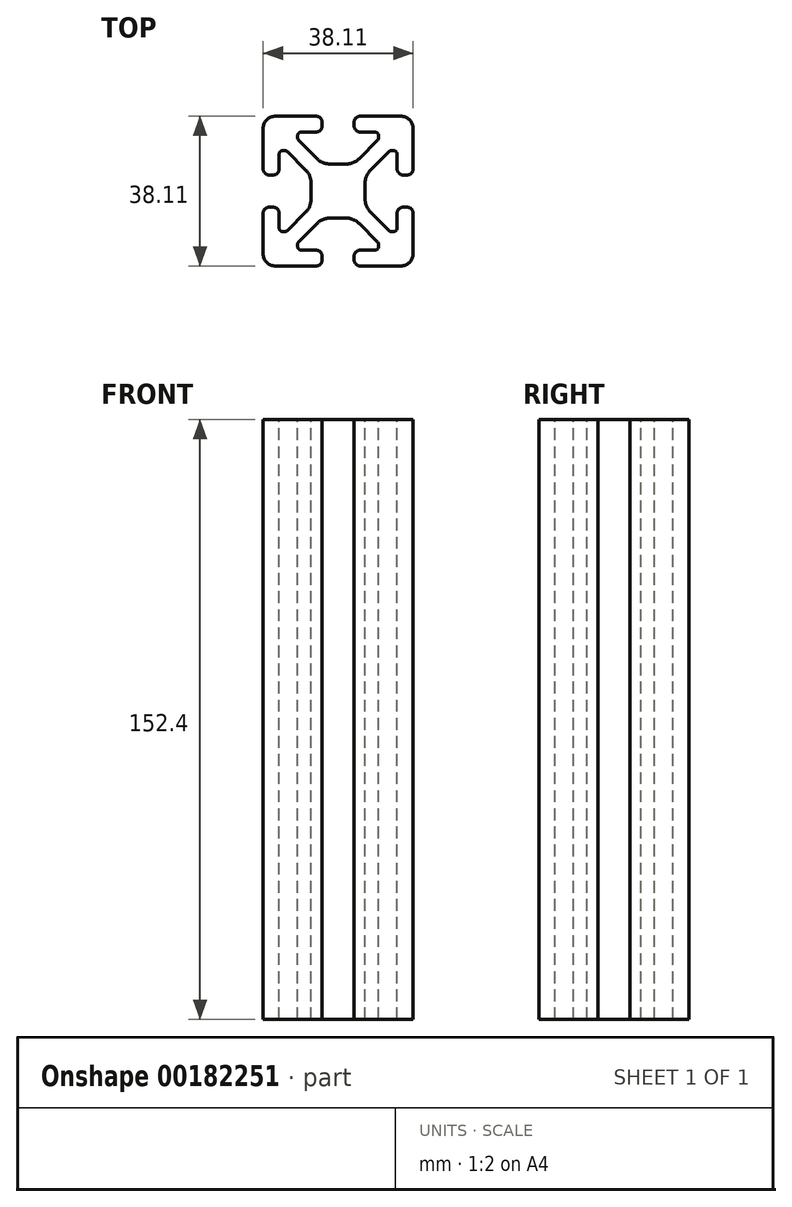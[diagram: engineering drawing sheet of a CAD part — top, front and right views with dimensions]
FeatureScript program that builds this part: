
annotation { "Feature Type Name" : "Feature", "Feature Type Description" : "" }
export const myFeature = defineFeature(function(context is Context, id is Id, definition is map)
    precondition{}
    {
        {
            var Q0;
            Q0=qCreatedBy(makeId("Top.planeOp"),FACE);
            var sketch = newSketch(context, id + "F0", { "sketchPlane" : qUnion([Q0])});
            skLineSegment(sketch, "E0.0", {"start": v(-3.18, 31.75) * mm, "end": v(-3.18, 21.51) * mm});
            skArc(sketch, "E1.0", {"start": v(0, 34.93) * mm, "mid": v(-2.25, 34) * mm, "end": v(-3.18, 31.75) * mm});
            skArc(sketch, "E2.0", {"start": v(-3.18, 21.51) * mm, "mid": v(-2.71, 20.4) * mm, "end": v(-1.6, 19.94) * mm});
            skLineSegment(sketch, "E3.0", {"start": v(-1.6, 19.94) * mm, "end": v(-0.69, 19.94) * mm});
            skArc(sketch, "E4.0", {"start": v(-0.69, 19.94) * mm, "mid": v(0.43, 20.4) * mm, "end": v(0.89, 21.51) * mm});
            skLineSegment(sketch, "E5.0", {"start": v(0.89, 21.51) * mm, "end": v(0.89, 25.27) * mm});
            skArc(sketch, "E6.0", {"start": v(0.89, 25.27) * mm, "mid": v(1.15, 25.9) * mm, "end": v(1.78, 26.16) * mm});
            skLineSegment(sketch, "E7.0", {"start": v(1.78, 26.16) * mm, "end": v(2.35, 26.16) * mm});
            skArc(sketch, "E8.0", {"start": v(2.35, 26.16) * mm, "mid": v(2.69, 26.1) * mm, "end": v(2.97, 25.9) * mm});
            skLineSegment(sketch, "E9.0", {"start": v(2.97, 25.9) * mm, "end": v(7.61, 21.26) * mm});
            skArc(sketch, "E10.0", {"start": v(7.61, 21.26) * mm, "mid": v(8.64, 19.72) * mm, "end": v(9, 17.9) * mm});
            skLineSegment(sketch, "E11.0", {"start": v(9, 17.9) * mm, "end": v(9, 13.85) * mm});
            skArc(sketch, "E12.0", {"start": v(9, 13.85) * mm, "mid": v(8.64, 12.03) * mm, "end": v(7.61, 10.49) * mm});
            skLineSegment(sketch, "E13.0", {"start": v(7.61, 10.49) * mm, "end": v(2.97, 5.85) * mm});
            skArc(sketch, "E14.0", {"start": v(2.97, 5.85) * mm, "mid": v(2.69, 5.66) * mm, "end": v(2.35, 5.59) * mm});
            skLineSegment(sketch, "E15.0", {"start": v(2.35, 5.59) * mm, "end": v(1.78, 5.59) * mm});
            skArc(sketch, "E16.0", {"start": v(1.78, 5.59) * mm, "mid": v(1.15, 5.85) * mm, "end": v(0.89, 6.48) * mm});
            skLineSegment(sketch, "E17.0", {"start": v(0.89, 6.48) * mm, "end": v(0.89, 10.24) * mm});
            skArc(sketch, "E18.0", {"start": v(0.89, 10.24) * mm, "mid": v(0.43, 11.35) * mm, "end": v(-0.69, 11.81) * mm});
            skLineSegment(sketch, "E19.0", {"start": v(-0.69, 11.81) * mm, "end": v(-1.6, 11.81) * mm});
            skArc(sketch, "E20.0", {"start": v(-1.6, 11.81) * mm, "mid": v(-2.71, 11.35) * mm, "end": v(-3.17, 10.24) * mm});
            skLineSegment(sketch, "E21.0", {"start": v(-3.17, 10.24) * mm, "end": v(-3.17, 0) * mm});
            skArc(sketch, "E22.0", {"start": v(-3.17, 0) * mm, "mid": v(-2.25, -2.25) * mm, "end": v(0, -3.17) * mm});
            skLineSegment(sketch, "E23.0", {"start": v(0, -3.17) * mm, "end": v(10.24, -3.17) * mm});
            skArc(sketch, "E24.0", {"start": v(10.24, -3.17) * mm, "mid": v(11.35, -2.71) * mm, "end": v(11.81, -1.6) * mm});
            skLineSegment(sketch, "E25.0", {"start": v(11.81, -1.6) * mm, "end": v(11.81, -0.69) * mm});
            skArc(sketch, "E26.0", {"start": v(11.81, -0.69) * mm, "mid": v(11.35, 0.43) * mm, "end": v(10.24, 0.89) * mm});
            skLineSegment(sketch, "E27.0", {"start": v(10.24, 0.89) * mm, "end": v(6.48, 0.89) * mm});
            skArc(sketch, "E28.0", {"start": v(6.48, 0.89) * mm, "mid": v(5.85, 1.15) * mm, "end": v(5.59, 1.78) * mm});
            skLineSegment(sketch, "E29.0", {"start": v(5.59, 1.78) * mm, "end": v(5.59, 2.35) * mm});
            skArc(sketch, "E30.0", {"start": v(5.59, 2.35) * mm, "mid": v(5.66, 2.69) * mm, "end": v(5.85, 2.97) * mm});
            skLineSegment(sketch, "E31.0", {"start": v(5.85, 2.97) * mm, "end": v(10.49, 7.61) * mm});
            skArc(sketch, "E32.0", {"start": v(10.49, 7.61) * mm, "mid": v(12.03, 8.64) * mm, "end": v(13.85, 9) * mm});
            skLineSegment(sketch, "E33.0", {"start": v(13.85, 9) * mm, "end": v(17.9, 9) * mm});
            skArc(sketch, "E34.0", {"start": v(17.9, 9) * mm, "mid": v(19.72, 8.64) * mm, "end": v(21.26, 7.61) * mm});
            skLineSegment(sketch, "E35.0", {"start": v(21.26, 7.61) * mm, "end": v(25.9, 2.97) * mm});
            skArc(sketch, "E36.0", {"start": v(25.9, 2.97) * mm, "mid": v(26.1, 2.69) * mm, "end": v(26.16, 2.35) * mm});
            skPoint(sketch, "E37.0", {"position": v(26.16, 1.78) * mm});
            skArc(sketch, "E38.0", {"start": v(26.16, 1.78) * mm, "mid": v(25.9, 1.15) * mm, "end": v(25.27, 0.89) * mm});
            skLineSegment(sketch, "E39.0", {"start": v(25.27, 0.89) * mm, "end": v(21.51, 0.89) * mm});
            skArc(sketch, "E40.0", {"start": v(21.51, 0.89) * mm, "mid": v(20.4, 0.43) * mm, "end": v(19.94, -0.69) * mm});
            skPoint(sketch, "E41.0", {"position": v(19.94, -1.6) * mm});
            skLineSegment(sketch, "E42.0", {"start": v(19.94, -0.69) * mm, "end": v(19.94, -1.6) * mm});
            skArc(sketch, "E43.0", {"start": v(19.94, -1.6) * mm, "mid": v(20.4, -2.71) * mm, "end": v(21.51, -3.17) * mm});
            skLineSegment(sketch, "E44.0", {"start": v(21.51, -3.17) * mm, "end": v(31.75, -3.17) * mm});
            skArc(sketch, "E45.0", {"start": v(31.75, -3.17) * mm, "mid": v(34, -2.25) * mm, "end": v(34.93, 0) * mm});
            skLineSegment(sketch, "E46.0", {"start": v(34.93, 0) * mm, "end": v(34.93, 10.24) * mm});
            skArc(sketch, "E47.0", {"start": v(34.93, 10.24) * mm, "mid": v(34.46, 11.35) * mm, "end": v(33.35, 11.81) * mm});
            skLineSegment(sketch, "E48.0", {"start": v(33.35, 11.81) * mm, "end": v(32.44, 11.81) * mm});
            skArc(sketch, "E49.0", {"start": v(32.44, 11.81) * mm, "mid": v(31.32, 11.35) * mm, "end": v(30.86, 10.24) * mm});
            skLineSegment(sketch, "E50.0", {"start": v(30.86, 10.24) * mm, "end": v(30.86, 6.48) * mm});
            skArc(sketch, "E51.0", {"start": v(30.86, 6.48) * mm, "mid": v(30.6, 5.85) * mm, "end": v(29.97, 5.59) * mm});
            skLineSegment(sketch, "E52.0", {"start": v(29.97, 5.59) * mm, "end": v(29.4, 5.59) * mm});
            skArc(sketch, "E53.0", {"start": v(29.4, 5.59) * mm, "mid": v(29.06, 5.66) * mm, "end": v(28.78, 5.85) * mm});
            skLineSegment(sketch, "E54.0", {"start": v(28.78, 5.85) * mm, "end": v(24.14, 10.49) * mm});
            skArc(sketch, "E55.0", {"start": v(24.14, 10.49) * mm, "mid": v(23.1, 12.03) * mm, "end": v(22.74, 13.85) * mm});
            skLineSegment(sketch, "E56.0", {"start": v(22.74, 13.85) * mm, "end": v(22.74, 17.9) * mm});
            skArc(sketch, "E57.0", {"start": v(22.74, 17.9) * mm, "mid": v(23.1, 19.72) * mm, "end": v(24.14, 21.26) * mm});
            skLineSegment(sketch, "E58.0", {"start": v(24.14, 21.26) * mm, "end": v(28.78, 25.9) * mm});
            skArc(sketch, "E59.0", {"start": v(28.78, 25.9) * mm, "mid": v(29.06, 26.1) * mm, "end": v(29.4, 26.16) * mm});
            skLineSegment(sketch, "E60.0", {"start": v(29.4, 26.16) * mm, "end": v(29.97, 26.16) * mm});
            skArc(sketch, "E61.0", {"start": v(29.97, 26.16) * mm, "mid": v(30.6, 25.9) * mm, "end": v(30.86, 25.27) * mm});
            skLineSegment(sketch, "E62.0", {"start": v(30.86, 25.27) * mm, "end": v(30.86, 21.51) * mm});
            skArc(sketch, "E63.0", {"start": v(30.86, 21.51) * mm, "mid": v(31.32, 20.4) * mm, "end": v(32.44, 19.94) * mm});
            skLineSegment(sketch, "E64.0", {"start": v(32.44, 19.94) * mm, "end": v(33.35, 19.94) * mm});
            skArc(sketch, "E65.0", {"start": v(33.35, 19.94) * mm, "mid": v(34.46, 20.4) * mm, "end": v(34.93, 21.51) * mm});
            skLineSegment(sketch, "E66.0", {"start": v(34.93, 21.51) * mm, "end": v(34.93, 31.75) * mm});
            skArc(sketch, "E67.0", {"start": v(34.93, 31.75) * mm, "mid": v(34, 34) * mm, "end": v(31.75, 34.93) * mm});
            skLineSegment(sketch, "E68.0", {"start": v(31.75, 34.93) * mm, "end": v(21.51, 34.93) * mm});
            skArc(sketch, "E69.0", {"start": v(21.51, 34.93) * mm, "mid": v(20.4, 34.46) * mm, "end": v(19.94, 33.35) * mm});
            skLineSegment(sketch, "E70.0", {"start": v(19.94, 33.35) * mm, "end": v(19.94, 32.44) * mm});
            skArc(sketch, "E71.0", {"start": v(19.94, 32.44) * mm, "mid": v(20.4, 31.32) * mm, "end": v(21.51, 30.86) * mm});
            skLineSegment(sketch, "E72.0", {"start": v(21.51, 30.86) * mm, "end": v(25.27, 30.86) * mm});
            skArc(sketch, "E73.0", {"start": v(25.27, 30.86) * mm, "mid": v(25.9, 30.6) * mm, "end": v(26.16, 29.97) * mm});
            skLineSegment(sketch, "E74.0", {"start": v(26.16, 29.97) * mm, "end": v(26.16, 29.4) * mm});
            skArc(sketch, "E75.0", {"start": v(26.16, 29.4) * mm, "mid": v(26.1, 29.06) * mm, "end": v(25.9, 28.78) * mm});
            skLineSegment(sketch, "E76.0", {"start": v(25.9, 28.78) * mm, "end": v(21.26, 24.14) * mm});
            skArc(sketch, "E77.0", {"start": v(11.81, 33.35) * mm, "mid": v(11.35, 34.46) * mm, "end": v(10.24, 34.93) * mm});
            skLineSegment(sketch, "E78.0", {"start": v(11.81, 32.44) * mm, "end": v(11.81, 33.35) * mm});
            skArc(sketch, "E79.0", {"start": v(10.24, 30.86) * mm, "mid": v(11.35, 31.32) * mm, "end": v(11.81, 32.44) * mm});
            skLineSegment(sketch, "E80.0", {"start": v(6.48, 30.86) * mm, "end": v(10.24, 30.86) * mm});
            skArc(sketch, "E81.0", {"start": v(5.59, 29.97) * mm, "mid": v(5.85, 30.6) * mm, "end": v(6.48, 30.86) * mm});
            skLineSegment(sketch, "E82.0", {"start": v(5.59, 29.4) * mm, "end": v(5.59, 29.97) * mm});
            skArc(sketch, "E83.0", {"start": v(5.85, 28.78) * mm, "mid": v(5.66, 29.06) * mm, "end": v(5.59, 29.4) * mm});
            skLineSegment(sketch, "E84.0", {"start": v(10.49, 24.14) * mm, "end": v(5.85, 28.78) * mm});
            skArc(sketch, "E85.0", {"start": v(13.85, 22.74) * mm, "mid": v(12.03, 23.1) * mm, "end": v(10.49, 24.14) * mm});
            skLineSegment(sketch, "E86.0", {"start": v(17.9, 22.74) * mm, "end": v(13.85, 22.74) * mm});
            skArc(sketch, "E87.0", {"start": v(21.26, 24.14) * mm, "mid": v(19.72, 23.1) * mm, "end": v(17.9, 22.74) * mm});
            skLineSegment(sketch, "E88.0", {"start": v(26.16, 2.35) * mm, "end": v(26.16, 1.78) * mm});
            skLineSegment(sketch, "E89", {"start": v(0, 34.93) * mm, "end": v(10.24, 34.93) * mm});
            skSolve(sketch);
        }
        {
            var Q0;
            Q0=qSketchRegion(id+"F0",true);
            extrude(context, id + "F1", {"entities" : qUnion([Q0]), "oppositeDirection" : true, "depth" : 152.4 * mm});
        }
    });
